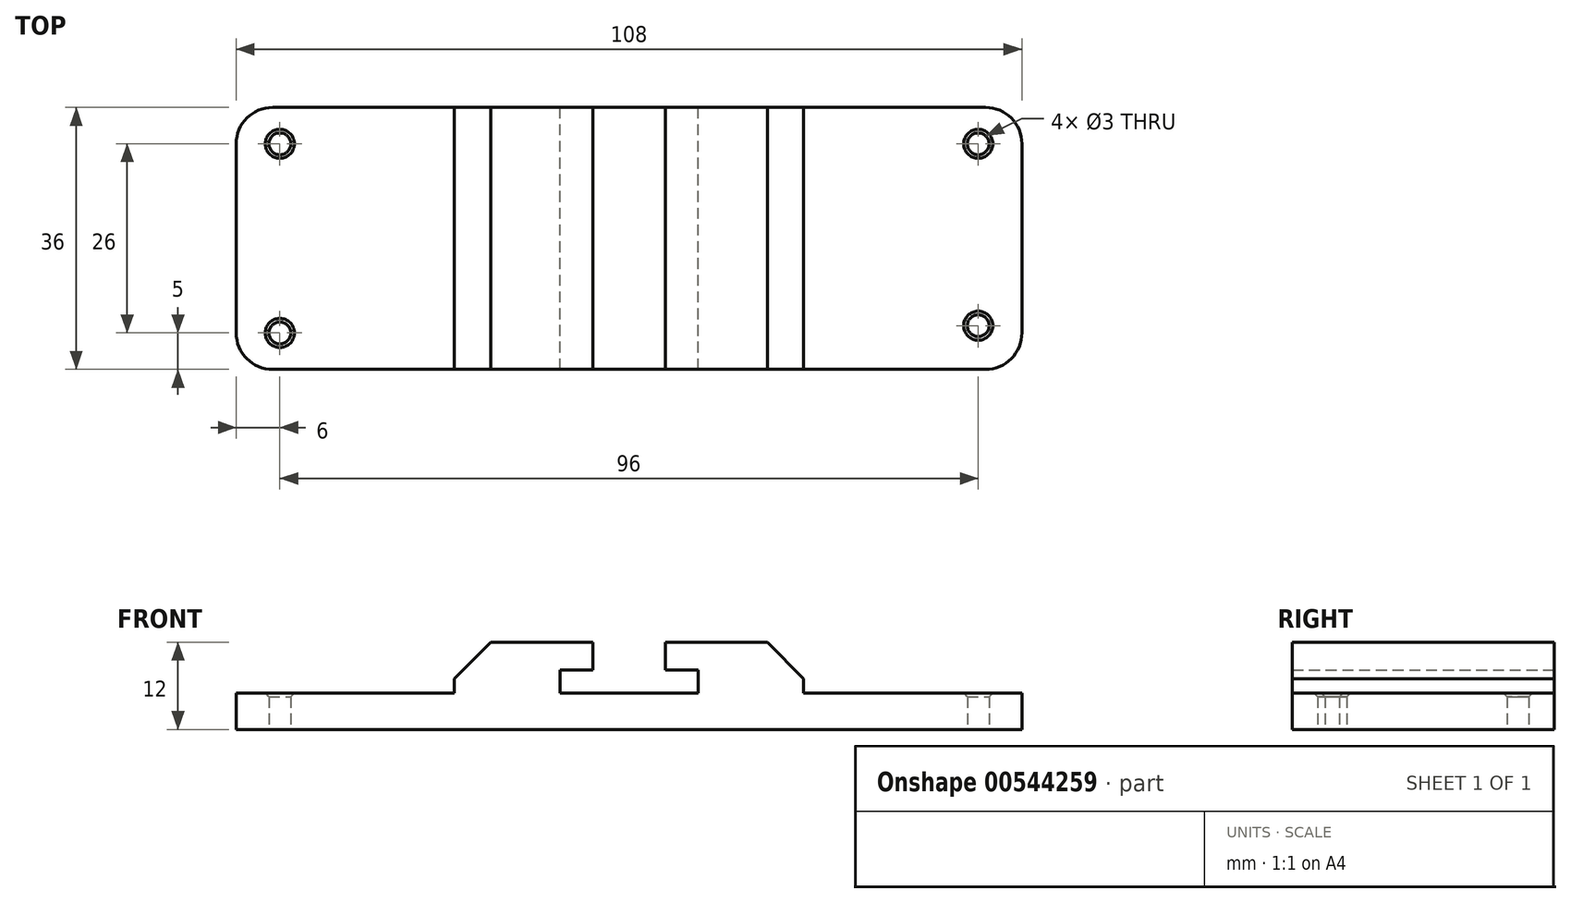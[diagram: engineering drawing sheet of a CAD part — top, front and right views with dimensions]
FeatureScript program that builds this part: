
annotation { "Feature Type Name" : "Feature", "Feature Type Description" : "" }
export const myFeature = defineFeature(function(context is Context, id is Id, definition is map)
    precondition{}
    {
        {
            var Q0;
            Q0=qCreatedBy(makeId("Front.planeOp"),FACE);
            var sketch = newSketch(context, id + "F0", { "sketchPlane" : qUnion([Q0])});
            skLineSegment(sketch, "E0", {"start": v(0, 0) * mm, "end": v(54, 0) * mm});
            skLineSegment(sketch, "E1", {"start": v(54, 0) * mm, "end": v(54, 5) * mm});
            skLineSegment(sketch, "E2", {"start": v(54, 5) * mm, "end": v(24, 5) * mm});
            skLineSegment(sketch, "E3", {"start": v(24, 5) * mm, "end": v(24, 12) * mm});
            skLineSegment(sketch, "E4", {"start": v(5, 12) * mm, "end": v(5, 8.2) * mm});
            skLineSegment(sketch, "E5", {"start": v(9.5, 5) * mm, "end": v(9.5, 8.2) * mm});
            skLineSegment(sketch, "E6", {"start": v(9.5, 8.2) * mm, "end": v(5, 8.2) * mm});
            skLineSegment(sketch, "E7", {"start": v(9.5, 5) * mm, "end": v(0, 5) * mm});
            skLineSegment(sketch, "E8", {"start": v(5, 12) * mm, "end": v(24, 12) * mm});
            skLineSegment(sketch, "E9", {"start": v(0, 5) * mm, "end": v(-9.5, 5) * mm});
            skLineSegment(sketch, "E10", {"start": v(-9.5, 5) * mm, "end": v(-9.5, 8.2) * mm});
            skLineSegment(sketch, "E11", {"start": v(-9.5, 8.2) * mm, "end": v(-5, 8.2) * mm});
            skLineSegment(sketch, "E12", {"start": v(-5, 8.2) * mm, "end": v(-5, 12) * mm});
            skLineSegment(sketch, "E13", {"start": v(-5, 12) * mm, "end": v(-24, 12) * mm});
            skLineSegment(sketch, "E14", {"start": v(-24, 12) * mm, "end": v(-24, 5) * mm});
            skLineSegment(sketch, "E15", {"start": v(-24, 5) * mm, "end": v(-54, 5) * mm});
            skLineSegment(sketch, "E16", {"start": v(-54, 5) * mm, "end": v(-54, 0) * mm});
            skLineSegment(sketch, "E17", {"start": v(-54, 0) * mm, "end": v(0, 0) * mm});
            skSolve(sketch);
        }
        {
            var Q0;
            Q0=makeQuery(id+"F0.imprint","IMPRINT",FACE,{"disambiguationData":[TD([[makeQuery(id+"F0.imprint","IMPRINT",EDGE,{"derivedFrom":sQuery(id+"F0.wireOp",EDGE,"E0")}),1.0]])]});
            extrude(context, id + "F1", {"entities" : qUnion([Q0]), "depth" : 36 * mm, "offsetDistance" : 25 * mm});
        }
        {
            var Q0;
            Q0=makeQuery(id+"F1.opExtrude","SWEPT_EDGE",EDGE,{"disambiguationData":[OSD([sQuery(id+"F0.wireOp",EDGE,"E3"),sQuery(id+"F0.wireOp",EDGE,"E8")])]});
            var Q1;
            Q1=makeQuery(id+"F1.opExtrude","SWEPT_EDGE",EDGE,{"disambiguationData":[OSD([sQuery(id+"F0.wireOp",EDGE,"E13"),sQuery(id+"F0.wireOp",EDGE,"E14")])]});
            chamfer(context, id + "F2", {"entities" : qUnion([Q0, Q1]), "width" : 5 * mm, "tangentPropagation" : true});
        }
        {
            var Q0;
            Q0=qCreatedBy(makeId("Top.planeOp"),FACE);
            var sketch = newSketch(context, id + "F3", { "sketchPlane" : qUnion([Q0])});
            skCircle(sketch, "E18", {"center": v(-48, -5) * mm, "radius": 1.5 * mm});
            skCircle(sketch, "E19", {"center": v(-48, -31) * mm, "radius": 1.5 * mm});
            skCircle(sketch, "E20", {"center": v(48, -5) * mm, "radius": 1.5 * mm});
            skCircle(sketch, "E21", {"center": v(48, -30) * mm, "radius": 1.5 * mm});
            skSolve(sketch);
        }
        {
            var Q0;
            Q0 = qSketchRegion(id + "F3", true);
            extrude(context, id + "F4", {"entities" : qUnion([Q0]), "operationType" : NewBodyOperationType.REMOVE, "depth" : 13.1 * mm, "offsetDistance" : 25 * mm});
        }
        {
            var Q0;
            Q0=makeQuery(id+"F4.boolean.opBoolean","INTERSECT",EDGE,{"derivedFrom":[makeQuery(id+"F1.opExtrude","SWEPT_FACE",FACE,{"disambiguationData":[OSD([sQuery(id+"F0.wireOp",EDGE,"E15")])]}),makeQuery(id+"F4.opExtrude","SWEPT_FACE",FACE,{"disambiguationData":[OSD([sQuery(id+"F3.wireOp",EDGE,"E18")])]})]});
            var Q1;
            Q1=makeQuery(id+"F4.boolean.opBoolean","INTERSECT",EDGE,{"derivedFrom":[makeQuery(id+"F1.opExtrude","SWEPT_FACE",FACE,{"disambiguationData":[OSD([sQuery(id+"F0.wireOp",EDGE,"E15")])]}),makeQuery(id+"F4.opExtrude","SWEPT_FACE",FACE,{"disambiguationData":[OSD([sQuery(id+"F3.wireOp",EDGE,"E19")])]})]});
            var Q2;
            Q2=makeQuery(id+"F4.boolean.opBoolean","INTERSECT",EDGE,{"derivedFrom":[makeQuery(id+"F1.opExtrude","SWEPT_FACE",FACE,{"disambiguationData":[OSD([sQuery(id+"F0.wireOp",EDGE,"E2")])]}),makeQuery(id+"F4.opExtrude","SWEPT_FACE",FACE,{"disambiguationData":[OSD([sQuery(id+"F3.wireOp",EDGE,"E20")])]})]});
            var Q3;
            Q3=makeQuery(id+"F4.boolean.opBoolean","INTERSECT",EDGE,{"derivedFrom":[makeQuery(id+"F1.opExtrude","SWEPT_FACE",FACE,{"disambiguationData":[OSD([sQuery(id+"F0.wireOp",EDGE,"E2")])]}),makeQuery(id+"F4.opExtrude","SWEPT_FACE",FACE,{"disambiguationData":[OSD([sQuery(id+"F3.wireOp",EDGE,"E21")])]})]});
            chamfer(context, id + "F5", {"entities" : qUnion([Q0, Q1, Q2, Q3]), "width" : 0.5 * mm, "tangentPropagation" : true});
        }
        {
            var Q0;
            Q0=makeQuery(id+"F1.opExtrude","CAP_EDGE",EDGE,{"disambiguationData":[OSD([sQuery(id+"F0.wireOp",EDGE,"E16")])],"isStart":true});
            var Q1;
            Q1=makeQuery(id+"F1.opExtrude","CAP_EDGE",EDGE,{"disambiguationData":[OSD([sQuery(id+"F0.wireOp",EDGE,"E16")])],"isStart":false});
            var Q2;
            Q2=makeQuery(id+"F1.opExtrude","CAP_EDGE",EDGE,{"disambiguationData":[OSD([sQuery(id+"F0.wireOp",EDGE,"E1")])],"isStart":false});
            var Q3;
            Q3=makeQuery(id+"F1.opExtrude","CAP_EDGE",EDGE,{"disambiguationData":[OSD([sQuery(id+"F0.wireOp",EDGE,"E1")])],"isStart":true});
            fillet(context, id + "F6", {"entities" : qUnion([Q0, Q1, Q2, Q3]), "radius" : 5 * mm, "tangentPropagation" : true, "allowEdgeOverflow" : false});
        }
    });
